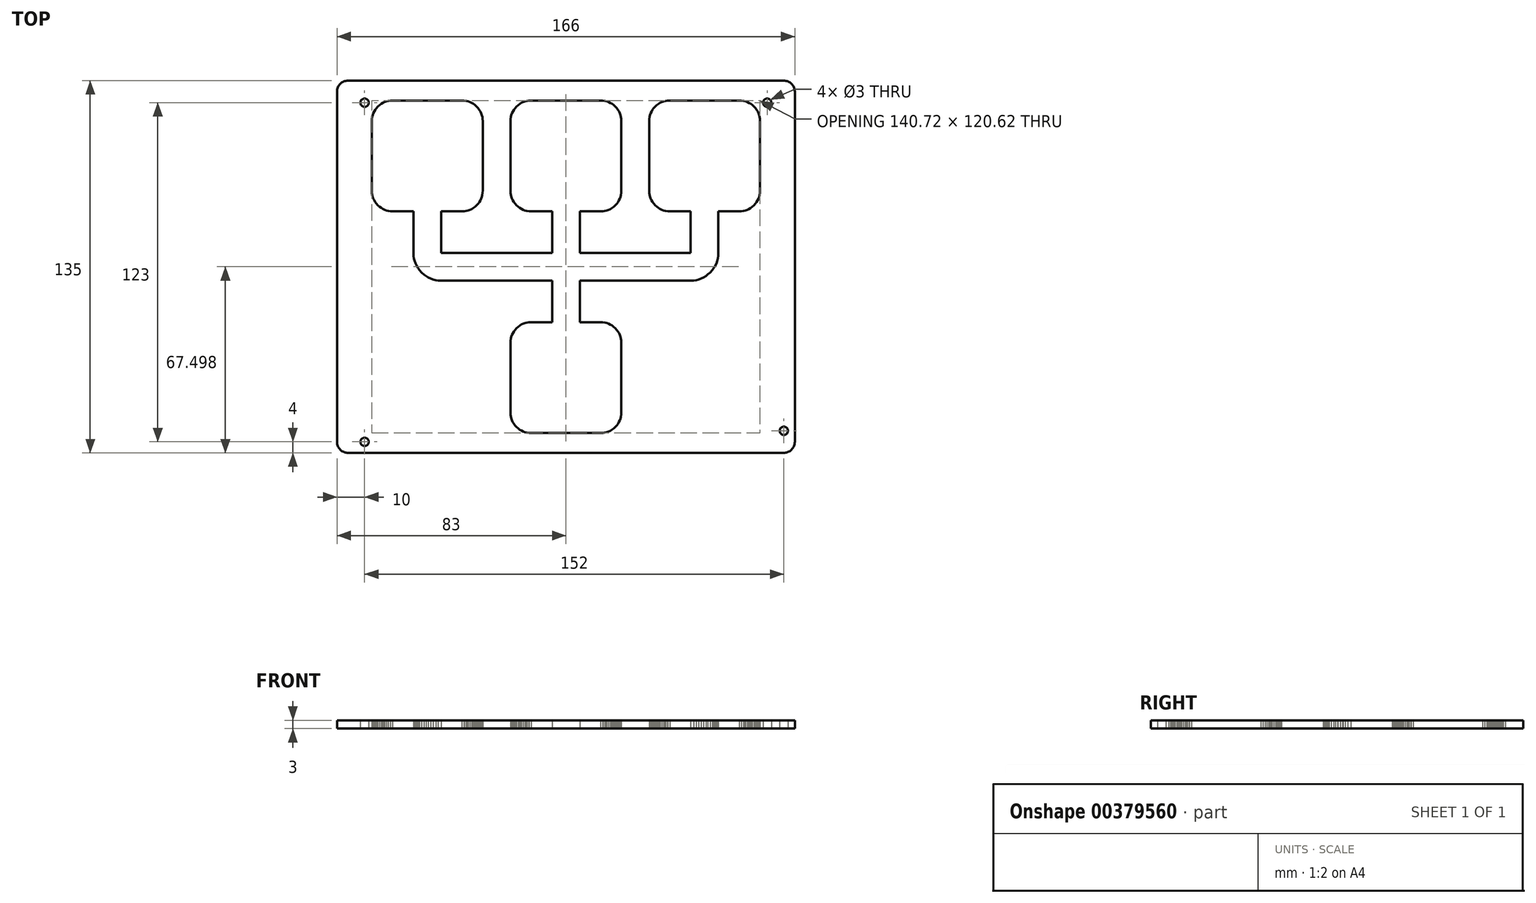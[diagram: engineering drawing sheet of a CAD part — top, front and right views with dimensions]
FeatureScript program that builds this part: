
annotation { "Feature Type Name" : "Feature", "Feature Type Description" : "" }
export const myFeature = defineFeature(function(context is Context, id is Id, definition is map)
    precondition{}
    {
        {
            var Q0;
            Q0=qCreatedBy(makeId("Top.planeOp"),FACE);
            var sketch = newSketch(context, id + "F0", { "sketchPlane" : qUnion([Q0])});
            skLineSegment(sketch, "E0.bottom", {"start": v(79, 67.5) * mm, "end": v(-79, 67.5) * mm});
            skLineSegment(sketch, "E0.top", {"start": v(79, -67.5) * mm, "end": v(-79, -67.5) * mm});
            skLineSegment(sketch, "E0.left", {"start": v(83, 63.5) * mm, "end": v(83, -63.5) * mm});
            skLineSegment(sketch, "E0.right", {"start": v(-83, 63.5) * mm, "end": v(-83, -63.5) * mm});
            skPoint(sketch, "E0.middle", {"position": v(0, 0) * mm});
            skLineSegment(sketch, "E1", {"start": v(0, 86.64) * mm, "end": v(0, -82.26) * mm, "construction": true});
            skLineSegment(sketch, "E2", {"start": v(-88.3, 0) * mm, "end": v(88.19, 0) * mm, "construction": true});
            skPoint(sketch, "E2.endSnap0", {"position": v(-83, 0) * mm});
            skLineSegment(sketch, "E3", {"start": v(-79, 72) * mm, "end": v(-79, -72.22) * mm, "construction": true});
            skLineSegment(sketch, "E4.MirrorCS", {"start": v(79, 72) * mm, "end": v(79, -72.22) * mm, "construction": true});
            skPoint(sketch, "E5.visualSharp", {"position": v(-83, 67.5) * mm});
            skArc(sketch, "E5.filletArc", {"start": v(-79, 67.5) * mm, "mid": v(-81.83, 66.33) * mm, "end": v(-83, 63.5) * mm});
            skPoint(sketch, "E6.visualSharp", {"position": v(83, 67.5) * mm});
            skArc(sketch, "E6.filletArc", {"start": v(83, 63.5) * mm, "mid": v(81.83, 66.33) * mm, "end": v(79, 67.5) * mm});
            skPoint(sketch, "E7.visualSharp", {"position": v(83, -67.5) * mm});
            skArc(sketch, "E7.filletArc", {"start": v(79, -67.5) * mm, "mid": v(81.83, -66.33) * mm, "end": v(83, -63.5) * mm});
            skPoint(sketch, "E8.visualSharp", {"position": v(-83, -67.5) * mm});
            skArc(sketch, "E8.filletArc", {"start": v(-83, -63.5) * mm, "mid": v(-81.83, -66.33) * mm, "end": v(-79, -67.5) * mm});
            skLineSegment(sketch, "E9", {"start": v(-20.1, -52.77) * mm, "end": v(-20.06, -53.63) * mm});
            skLineSegment(sketch, "E10", {"start": v(-20.06, -53.63) * mm, "end": v(-19.96, -54.3) * mm});
            skLineSegment(sketch, "E11", {"start": v(-51.45, -2.81) * mm, "end": v(-50.73, -3.36) * mm});
            skLineSegment(sketch, "E12", {"start": v(-14.73, -20.4) * mm, "end": v(-15.49, -20.66) * mm});
            skLineSegment(sketch, "E13", {"start": v(-19.96, -54.3) * mm, "end": v(-19.8, -54.94) * mm});
            skLineSegment(sketch, "E14", {"start": v(-53.05, -1.2) * mm, "end": v(-52.3, -2.04) * mm});
            skLineSegment(sketch, "E15", {"start": v(-53.6, -0.49) * mm, "end": v(-53.05, -1.2) * mm});
            skLineSegment(sketch, "E16", {"start": v(-54.53, 1.2) * mm, "end": v(-54.15, 0.42) * mm});
            skLineSegment(sketch, "E17", {"start": v(-49.98, -3.82) * mm, "end": v(-49.01, -4.3) * mm});
            skLineSegment(sketch, "E18", {"start": v(-16.08, -20.94) * mm, "end": v(-16.64, -21.28) * mm});
            skLineSegment(sketch, "E19", {"start": v(-18.47, -22.93) * mm, "end": v(-18.87, -23.47) * mm});
            skLineSegment(sketch, "E20", {"start": v(-19.8, -54.94) * mm, "end": v(-19.55, -55.7) * mm});
            skLineSegment(sketch, "E21", {"start": v(-19.27, -56.28) * mm, "end": v(-18.93, -56.85) * mm});
            skLineSegment(sketch, "E22", {"start": v(-15.49, -20.66) * mm, "end": v(-16.08, -20.94) * mm});
            skLineSegment(sketch, "E23", {"start": v(-17.34, -21.79) * mm, "end": v(-17.9, -22.3) * mm});
            skLineSegment(sketch, "E24", {"start": v(-18.93, -56.85) * mm, "end": v(-18.42, -57.55) * mm});
            skLineSegment(sketch, "E25", {"start": v(-55.22, 3.92) * mm, "end": v(-55.1, 3.04) * mm});
            skLineSegment(sketch, "E26", {"start": v(-46.32, -4.97) * mm, "end": v(-45.23, -5.03) * mm});
            skLineSegment(sketch, "E27", {"start": v(-45.23, -5.03) * mm, "end": v(-43.26, -5.03) * mm});
            skLineSegment(sketch, "E28", {"start": v(-43.26, -5.03) * mm, "end": v(-5.03, -5.03) * mm});
            skLineSegment(sketch, "E29", {"start": v(-12.56, -20.1) * mm, "end": v(-13.42, -20.15) * mm});
            skLineSegment(sketch, "E30", {"start": v(-5.03, -5.77) * mm, "end": v(-5.03, -20.1) * mm});
            skLineSegment(sketch, "E31", {"start": v(-19.55, -55.7) * mm, "end": v(-19.27, -56.28) * mm});
            skLineSegment(sketch, "E32", {"start": v(-55.1, 3.04) * mm, "end": v(-54.89, 2.2) * mm});
            skLineSegment(sketch, "E33", {"start": v(-52.3, -2.04) * mm, "end": v(-51.45, -2.81) * mm});
            skLineSegment(sketch, "E34", {"start": v(-5.03, -20.1) * mm, "end": v(-5.4, -20.1) * mm});
            skLineSegment(sketch, "E35", {"start": v(-50.73, -3.36) * mm, "end": v(-49.98, -3.82) * mm});
            skLineSegment(sketch, "E36", {"start": v(-13.42, -20.15) * mm, "end": v(-14.08, -20.24) * mm});
            skLineSegment(sketch, "E37", {"start": v(-17.9, -22.3) * mm, "end": v(-18.47, -22.93) * mm});
            skLineSegment(sketch, "E38", {"start": v(-18.87, -23.47) * mm, "end": v(-19.21, -24.03) * mm});
            skLineSegment(sketch, "E39", {"start": v(-16.64, -21.28) * mm, "end": v(-17.34, -21.79) * mm});
            skLineSegment(sketch, "E40", {"start": v(-54.15, 0.42) * mm, "end": v(-53.6, -0.49) * mm});
            skLineSegment(sketch, "E41", {"start": v(-49.01, -4.3) * mm, "end": v(-48.2, -4.59) * mm});
            skLineSegment(sketch, "E42", {"start": v(-5.03, -5.03) * mm, "end": v(-5.03, -5.77) * mm});
            skLineSegment(sketch, "E43", {"start": v(-54.89, 2.2) * mm, "end": v(-54.53, 1.2) * mm});
            skLineSegment(sketch, "E44", {"start": v(-5.4, -20.1) * mm, "end": v(-12.56, -20.1) * mm});
            skLineSegment(sketch, "E45", {"start": v(-47.2, -4.84) * mm, "end": v(-46.32, -4.97) * mm});
            skLineSegment(sketch, "E46", {"start": v(-14.08, -20.24) * mm, "end": v(-14.73, -20.4) * mm});
            skLineSegment(sketch, "E47", {"start": v(-19.56, -24.75) * mm, "end": v(-19.78, -25.37) * mm});
            skLineSegment(sketch, "E48", {"start": v(-19.78, -25.37) * mm, "end": v(-19.93, -26) * mm});
            skLineSegment(sketch, "E49", {"start": v(-19.93, -26) * mm, "end": v(-20.07, -26.87) * mm});
            skLineSegment(sketch, "E50", {"start": v(-20.07, -26.87) * mm, "end": v(-20.1, -27.64) * mm});
            skLineSegment(sketch, "E51", {"start": v(-20.1, -27.64) * mm, "end": v(-20.1, -28.87) * mm});
            skLineSegment(sketch, "E52", {"start": v(-19.21, -24.03) * mm, "end": v(-19.56, -24.75) * mm});
            skLineSegment(sketch, "E53", {"start": v(-48.2, -4.59) * mm, "end": v(-47.2, -4.84) * mm});
            skLineSegment(sketch, "E54", {"start": v(-20.1, -28.87) * mm, "end": v(-20.1, -52.77) * mm});
            skLineSegment(sketch, "E55", {"start": v(12.56, -60.31) * mm, "end": v(13.42, -60.27) * mm});
            skLineSegment(sketch, "E56", {"start": v(19.93, -54.4) * mm, "end": v(20.07, -53.54) * mm});
            skLineSegment(sketch, "E57", {"start": v(16.74, -21.34) * mm, "end": v(16.18, -21) * mm});
            skLineSegment(sketch, "E58", {"start": v(-13.33, -60.28) * mm, "end": v(-12.56, -60.31) * mm});
            skLineSegment(sketch, "E59", {"start": v(13.42, -60.27) * mm, "end": v(14.09, -60.17) * mm});
            skLineSegment(sketch, "E60", {"start": v(17.34, -58.63) * mm, "end": v(17.9, -58.11) * mm});
            skLineSegment(sketch, "E61", {"start": v(17.9, -22.3) * mm, "end": v(17.28, -21.74) * mm});
            skLineSegment(sketch, "E62", {"start": v(16.64, -59.13) * mm, "end": v(17.34, -58.63) * mm});
            skLineSegment(sketch, "E63", {"start": v(5.03, -5.03) * mm, "end": v(7, -5.03) * mm});
            skLineSegment(sketch, "E64", {"start": v(49.06, -4.27) * mm, "end": v(49.84, -3.9) * mm});
            skLineSegment(sketch, "E65", {"start": v(53.07, -1.2) * mm, "end": v(53.62, -0.47) * mm});
            skLineSegment(sketch, "E66", {"start": v(18.47, -57.48) * mm, "end": v(18.87, -56.95) * mm});
            skLineSegment(sketch, "E67", {"start": v(20.1, -51.54) * mm, "end": v(20.1, -27.64) * mm});
            skLineSegment(sketch, "E68", {"start": v(-17.9, -58.11) * mm, "end": v(-17.27, -58.68) * mm});
            skLineSegment(sketch, "E69", {"start": v(15.46, -20.65) * mm, "end": v(14.84, -20.43) * mm});
            skLineSegment(sketch, "E70", {"start": v(54.08, 0.28) * mm, "end": v(54.55, 1.24) * mm});
            skLineSegment(sketch, "E71", {"start": v(54.55, 1.24) * mm, "end": v(54.84, 2.05) * mm});
            skLineSegment(sketch, "E72", {"start": v(7, -5.03) * mm, "end": v(45.23, -5.03) * mm});
            skLineSegment(sketch, "E73", {"start": v(14.2, -20.28) * mm, "end": v(13.34, -20.14) * mm});
            skLineSegment(sketch, "E74", {"start": v(-16.74, -59.08) * mm, "end": v(-16.18, -59.42) * mm});
            skLineSegment(sketch, "E75", {"start": v(-14.2, -60.14) * mm, "end": v(-13.33, -60.28) * mm});
            skLineSegment(sketch, "E76", {"start": v(-14.84, -59.98) * mm, "end": v(-14.2, -60.14) * mm});
            skLineSegment(sketch, "E77", {"start": v(19.21, -56.38) * mm, "end": v(19.56, -55.66) * mm});
            skLineSegment(sketch, "E78", {"start": v(18.42, -22.87) * mm, "end": v(17.9, -22.3) * mm});
            skLineSegment(sketch, "E79", {"start": v(17.28, -21.74) * mm, "end": v(16.74, -21.34) * mm});
            skLineSegment(sketch, "E80", {"start": v(12.2, -20.1) * mm, "end": v(5.03, -20.1) * mm});
            skLineSegment(sketch, "E81", {"start": v(5.03, -20.1) * mm, "end": v(5.03, -19.37) * mm});
            skLineSegment(sketch, "E82", {"start": v(49.84, -3.9) * mm, "end": v(50.75, -3.34) * mm});
            skLineSegment(sketch, "E83", {"start": v(20.07, -53.54) * mm, "end": v(20.1, -52.77) * mm});
            skLineSegment(sketch, "E84", {"start": v(13.34, -20.14) * mm, "end": v(12.56, -20.1) * mm});
            skLineSegment(sketch, "E85", {"start": v(50.75, -3.34) * mm, "end": v(51.47, -2.8) * mm});
            skLineSegment(sketch, "E86", {"start": v(46.34, -4.97) * mm, "end": v(47.22, -4.84) * mm});
            skLineSegment(sketch, "E87", {"start": v(45.23, -5.03) * mm, "end": v(46.34, -4.97) * mm});
            skLineSegment(sketch, "E88", {"start": v(51.47, -2.8) * mm, "end": v(52.3, -2.04) * mm});
            skLineSegment(sketch, "E89", {"start": v(53.62, -0.47) * mm, "end": v(54.08, 0.28) * mm});
            skLineSegment(sketch, "E90", {"start": v(19.56, -55.66) * mm, "end": v(19.78, -55.05) * mm});
            skLineSegment(sketch, "E91", {"start": v(-15.45, -59.77) * mm, "end": v(-14.84, -59.98) * mm});
            skLineSegment(sketch, "E92", {"start": v(17.9, -58.11) * mm, "end": v(18.47, -57.48) * mm});
            skLineSegment(sketch, "E93", {"start": v(16.08, -59.48) * mm, "end": v(16.64, -59.13) * mm});
            skLineSegment(sketch, "E94", {"start": v(19.78, -55.05) * mm, "end": v(19.93, -54.4) * mm});
            skLineSegment(sketch, "E95", {"start": v(-18.42, -57.55) * mm, "end": v(-17.9, -58.11) * mm});
            skLineSegment(sketch, "E96", {"start": v(-17.27, -58.68) * mm, "end": v(-16.74, -59.08) * mm});
            skLineSegment(sketch, "E97", {"start": v(-16.18, -59.42) * mm, "end": v(-15.45, -59.77) * mm});
            skLineSegment(sketch, "E98", {"start": v(19.81, -25.48) * mm, "end": v(19.55, -24.72) * mm});
            skLineSegment(sketch, "E99", {"start": v(20.1, -27.64) * mm, "end": v(20.06, -26.79) * mm});
            skLineSegment(sketch, "E100", {"start": v(19.55, -24.72) * mm, "end": v(19.27, -24.13) * mm});
            skLineSegment(sketch, "E101", {"start": v(12.56, -20.1) * mm, "end": v(12.2, -20.1) * mm});
            skLineSegment(sketch, "E102", {"start": v(14.09, -60.17) * mm, "end": v(14.73, -60.02) * mm});
            skLineSegment(sketch, "E103", {"start": v(18.87, -56.95) * mm, "end": v(19.21, -56.38) * mm});
            skLineSegment(sketch, "E104", {"start": v(20.06, -26.79) * mm, "end": v(19.97, -26.12) * mm});
            skLineSegment(sketch, "E105", {"start": v(19.97, -26.12) * mm, "end": v(19.81, -25.48) * mm});
            skLineSegment(sketch, "E106", {"start": v(-11.33, -60.31) * mm, "end": v(12.56, -60.31) * mm});
            skLineSegment(sketch, "E107", {"start": v(14.73, -60.02) * mm, "end": v(15.49, -59.75) * mm});
            skLineSegment(sketch, "E108", {"start": v(5.03, -19.37) * mm, "end": v(5.03, -5.03) * mm});
            skLineSegment(sketch, "E109", {"start": v(19.27, -24.13) * mm, "end": v(18.93, -23.57) * mm});
            skLineSegment(sketch, "E110", {"start": v(18.93, -23.57) * mm, "end": v(18.42, -22.87) * mm});
            skLineSegment(sketch, "E111", {"start": v(14.84, -20.43) * mm, "end": v(14.2, -20.28) * mm});
            skLineSegment(sketch, "E112", {"start": v(48.06, -4.63) * mm, "end": v(49.06, -4.27) * mm});
            skLineSegment(sketch, "E113", {"start": v(47.22, -4.84) * mm, "end": v(48.06, -4.63) * mm});
            skLineSegment(sketch, "E114", {"start": v(52.3, -2.04) * mm, "end": v(53.07, -1.2) * mm});
            skLineSegment(sketch, "E115", {"start": v(-12.56, -60.31) * mm, "end": v(-11.33, -60.31) * mm});
            skLineSegment(sketch, "E116", {"start": v(20.1, -52.77) * mm, "end": v(20.1, -51.54) * mm});
            skLineSegment(sketch, "E117", {"start": v(16.18, -21) * mm, "end": v(15.46, -20.65) * mm});
            skLineSegment(sketch, "E118", {"start": v(15.49, -59.75) * mm, "end": v(16.08, -59.48) * mm});
            skLineSegment(sketch, "E119", {"start": v(70.07, 54.93) * mm, "end": v(69.8, 55.7) * mm});
            skLineSegment(sketch, "E120", {"start": v(69.53, 56.28) * mm, "end": v(69.18, 56.84) * mm});
            skLineSegment(sketch, "E121", {"start": v(55.23, 3.94) * mm, "end": v(55.28, 5.02) * mm});
            skLineSegment(sketch, "E122", {"start": v(54.84, 2.05) * mm, "end": v(55.1, 3.07) * mm});
            skLineSegment(sketch, "E123", {"start": v(62.82, 20.1) * mm, "end": v(63.68, 20.15) * mm});
            skLineSegment(sketch, "E124", {"start": v(69.82, 24.75) * mm, "end": v(70.04, 25.37) * mm});
            skLineSegment(sketch, "E125", {"start": v(65.1, 59.98) * mm, "end": v(64.46, 60.14) * mm});
            skLineSegment(sketch, "E126", {"start": v(61.6, 60.3) * mm, "end": v(37.7, 60.3) * mm});
            skLineSegment(sketch, "E127", {"start": v(69.18, 56.84) * mm, "end": v(68.68, 57.55) * mm});
            skLineSegment(sketch, "E128", {"start": v(70.04, 25.37) * mm, "end": v(70.19, 26) * mm});
            skLineSegment(sketch, "E129", {"start": v(66.34, 20.94) * mm, "end": v(66.9, 21.28) * mm});
            skLineSegment(sketch, "E130", {"start": v(55.65, 20.1) * mm, "end": v(62.82, 20.1) * mm});
            skLineSegment(sketch, "E131", {"start": v(35.53, 60.01) * mm, "end": v(34.77, 59.75) * mm});
            skLineSegment(sketch, "E132", {"start": v(34.77, 59.75) * mm, "end": v(34.18, 59.47) * mm});
            skLineSegment(sketch, "E133", {"start": v(64.46, 60.14) * mm, "end": v(63.6, 60.27) * mm});
            skLineSegment(sketch, "E134", {"start": v(32.35, 58.11) * mm, "end": v(31.8, 57.48) * mm});
            skLineSegment(sketch, "E135", {"start": v(30.15, 52.77) * mm, "end": v(30.15, 51.54) * mm});
            skLineSegment(sketch, "E136", {"start": v(30.48, 55.04) * mm, "end": v(30.33, 54.4) * mm});
            skLineSegment(sketch, "E137", {"start": v(64.34, 20.24) * mm, "end": v(64.99, 20.4) * mm});
            skLineSegment(sketch, "E138", {"start": v(70.36, 28.87) * mm, "end": v(70.36, 52.77) * mm});
            skLineSegment(sketch, "E139", {"start": v(64.99, 20.4) * mm, "end": v(65.75, 20.66) * mm});
            skLineSegment(sketch, "E140", {"start": v(65.75, 20.66) * mm, "end": v(66.34, 20.94) * mm});
            skLineSegment(sketch, "E141", {"start": v(70.36, 52.77) * mm, "end": v(70.32, 53.62) * mm});
            skLineSegment(sketch, "E142", {"start": v(67.53, 58.67) * mm, "end": v(67, 59.08) * mm});
            skLineSegment(sketch, "E143", {"start": v(68.16, 58.11) * mm, "end": v(67.53, 58.67) * mm});
            skLineSegment(sketch, "E144", {"start": v(37.7, 60.3) * mm, "end": v(36.84, 60.26) * mm});
            skLineSegment(sketch, "E145", {"start": v(34.18, 59.47) * mm, "end": v(33.62, 59.13) * mm});
            skLineSegment(sketch, "E146", {"start": v(36.17, 60.17) * mm, "end": v(35.53, 60.01) * mm});
            skLineSegment(sketch, "E147", {"start": v(31.05, 56.38) * mm, "end": v(30.7, 55.66) * mm});
            skLineSegment(sketch, "E148", {"start": v(30.7, 55.66) * mm, "end": v(30.48, 55.04) * mm});
            skLineSegment(sketch, "E149", {"start": v(55.28, 5.02) * mm, "end": v(55.28, 5.76) * mm});
            skLineSegment(sketch, "E150", {"start": v(66.9, 21.28) * mm, "end": v(67.6, 21.78) * mm});
            skLineSegment(sketch, "E151", {"start": v(68.16, 22.3) * mm, "end": v(68.73, 22.93) * mm});
            skLineSegment(sketch, "E152", {"start": v(69.8, 55.7) * mm, "end": v(69.53, 56.28) * mm});
            skLineSegment(sketch, "E153", {"start": v(62.82, 60.3) * mm, "end": v(61.6, 60.3) * mm});
            skLineSegment(sketch, "E154", {"start": v(63.6, 60.27) * mm, "end": v(62.82, 60.3) * mm});
            skLineSegment(sketch, "E155", {"start": v(36.84, 60.26) * mm, "end": v(36.17, 60.17) * mm});
            skLineSegment(sketch, "E156", {"start": v(63.68, 20.15) * mm, "end": v(64.34, 20.24) * mm});
            skLineSegment(sketch, "E157", {"start": v(33.62, 59.13) * mm, "end": v(32.92, 58.63) * mm});
            skLineSegment(sketch, "E158", {"start": v(30.15, 51.54) * mm, "end": v(30.15, 27.64) * mm});
            skLineSegment(sketch, "E159", {"start": v(31.8, 57.48) * mm, "end": v(31.39, 56.94) * mm});
            skLineSegment(sketch, "E160", {"start": v(30.15, 27.64) * mm, "end": v(30.2, 26.79) * mm});
            skLineSegment(sketch, "E161", {"start": v(30.3, 26.12) * mm, "end": v(30.45, 25.48) * mm});
            skLineSegment(sketch, "E162", {"start": v(70.36, 27.64) * mm, "end": v(70.36, 28.87) * mm});
            skLineSegment(sketch, "E163", {"start": v(55.28, 20.1) * mm, "end": v(55.65, 20.1) * mm});
            skLineSegment(sketch, "E164", {"start": v(69.13, 23.47) * mm, "end": v(69.47, 24.03) * mm});
            skLineSegment(sketch, "E165", {"start": v(69.47, 24.03) * mm, "end": v(69.82, 24.75) * mm});
            skLineSegment(sketch, "E166", {"start": v(70.22, 54.3) * mm, "end": v(70.07, 54.93) * mm});
            skLineSegment(sketch, "E167", {"start": v(68.68, 57.55) * mm, "end": v(68.16, 58.11) * mm});
            skLineSegment(sketch, "E168", {"start": v(55.28, 5.76) * mm, "end": v(55.28, 20.1) * mm});
            skLineSegment(sketch, "E169", {"start": v(67.6, 21.78) * mm, "end": v(68.16, 22.3) * mm});
            skLineSegment(sketch, "E170", {"start": v(70.33, 26.87) * mm, "end": v(70.36, 27.64) * mm});
            skLineSegment(sketch, "E171", {"start": v(70.32, 53.62) * mm, "end": v(70.22, 54.3) * mm});
            skLineSegment(sketch, "E172", {"start": v(68.73, 22.93) * mm, "end": v(69.13, 23.47) * mm});
            skLineSegment(sketch, "E173", {"start": v(67, 59.08) * mm, "end": v(66.44, 59.42) * mm});
            skLineSegment(sketch, "E174", {"start": v(66.44, 59.42) * mm, "end": v(65.71, 59.76) * mm});
            skLineSegment(sketch, "E175", {"start": v(65.71, 59.76) * mm, "end": v(65.1, 59.98) * mm});
            skLineSegment(sketch, "E176", {"start": v(32.92, 58.63) * mm, "end": v(32.35, 58.11) * mm});
            skLineSegment(sketch, "E177", {"start": v(31.39, 56.94) * mm, "end": v(31.05, 56.38) * mm});
            skLineSegment(sketch, "E178", {"start": v(30.33, 54.4) * mm, "end": v(30.19, 53.54) * mm});
            skLineSegment(sketch, "E179", {"start": v(30.19, 53.54) * mm, "end": v(30.15, 52.77) * mm});
            skLineSegment(sketch, "E180", {"start": v(30.2, 26.79) * mm, "end": v(30.3, 26.12) * mm});
            skLineSegment(sketch, "E181", {"start": v(55.1, 3.07) * mm, "end": v(55.23, 3.94) * mm});
            skLineSegment(sketch, "E182", {"start": v(70.19, 26) * mm, "end": v(70.33, 26.87) * mm});
            skLineSegment(sketch, "E183", {"start": v(15.46, 59.76) * mm, "end": v(14.84, 59.98) * mm});
            skLineSegment(sketch, "E184", {"start": v(14.2, 60.14) * mm, "end": v(13.34, 60.27) * mm});
            skLineSegment(sketch, "E185", {"start": v(31.84, 22.86) * mm, "end": v(32.35, 22.3) * mm});
            skLineSegment(sketch, "E186", {"start": v(17.28, 58.67) * mm, "end": v(16.74, 59.08) * mm});
            skLineSegment(sketch, "E187", {"start": v(5.02, 5.76) * mm, "end": v(5.02, 20.1) * mm});
            skLineSegment(sketch, "E188", {"start": v(14.84, 59.98) * mm, "end": v(14.2, 60.14) * mm});
            skLineSegment(sketch, "E189", {"start": v(13.34, 60.27) * mm, "end": v(12.56, 60.3) * mm});
            skLineSegment(sketch, "E190", {"start": v(32.98, 21.74) * mm, "end": v(33.52, 21.33) * mm});
            skLineSegment(sketch, "E191", {"start": v(19.21, 24.03) * mm, "end": v(19.56, 24.75) * mm});
            skLineSegment(sketch, "E192", {"start": v(31, 24.13) * mm, "end": v(31.33, 23.57) * mm});
            skLineSegment(sketch, "E193", {"start": v(30.71, 24.72) * mm, "end": v(31, 24.13) * mm});
            skLineSegment(sketch, "E194", {"start": v(12.56, 60.3) * mm, "end": v(11.33, 60.3) * mm});
            skLineSegment(sketch, "E195", {"start": v(14.73, 20.4) * mm, "end": v(15.49, 20.66) * mm});
            skLineSegment(sketch, "E196", {"start": v(5.4, 20.1) * mm, "end": v(12.56, 20.1) * mm});
            skLineSegment(sketch, "E197", {"start": v(19.97, 54.3) * mm, "end": v(19.81, 54.93) * mm});
            skLineSegment(sketch, "E198", {"start": v(11.33, 60.3) * mm, "end": v(-12.56, 60.3) * mm});
            skLineSegment(sketch, "E199", {"start": v(-12.56, 60.3) * mm, "end": v(-13.42, 60.26) * mm});
            skLineSegment(sketch, "E200", {"start": v(-13.42, 60.26) * mm, "end": v(-14.08, 60.17) * mm});
            skLineSegment(sketch, "E201", {"start": v(5.02, 20.1) * mm, "end": v(5.4, 20.1) * mm});
            skLineSegment(sketch, "E202", {"start": v(13.42, 20.15) * mm, "end": v(14.09, 20.24) * mm});
            skLineSegment(sketch, "E203", {"start": v(19.55, 55.7) * mm, "end": v(19.27, 56.28) * mm});
            skLineSegment(sketch, "E204", {"start": v(18.42, 57.55) * mm, "end": v(17.9, 58.11) * mm});
            skLineSegment(sketch, "E205", {"start": v(17.9, 58.11) * mm, "end": v(17.28, 58.67) * mm});
            skLineSegment(sketch, "E206", {"start": v(36.06, 20.27) * mm, "end": v(36.92, 20.14) * mm});
            skLineSegment(sketch, "E207", {"start": v(36.92, 20.14) * mm, "end": v(37.7, 20.1) * mm});
            skLineSegment(sketch, "E208", {"start": v(35.42, 20.43) * mm, "end": v(36.06, 20.27) * mm});
            skLineSegment(sketch, "E209", {"start": v(20.1, 27.64) * mm, "end": v(20.1, 28.87) * mm});
            skLineSegment(sketch, "E210", {"start": v(20.1, 52.77) * mm, "end": v(20.06, 53.62) * mm});
            skLineSegment(sketch, "E211", {"start": v(-14.08, 60.17) * mm, "end": v(-14.73, 60.01) * mm});
            skLineSegment(sketch, "E212", {"start": v(45.23, 5.02) * mm, "end": v(43.26, 5.02) * mm});
            skLineSegment(sketch, "E213", {"start": v(-14.73, 60.01) * mm, "end": v(-15.49, 59.75) * mm});
            skLineSegment(sketch, "E214", {"start": v(38.06, 20.1) * mm, "end": v(45.23, 20.1) * mm});
            skLineSegment(sketch, "E215", {"start": v(-15.49, 59.75) * mm, "end": v(-16.07, 59.47) * mm});
            skLineSegment(sketch, "E216", {"start": v(31.33, 23.57) * mm, "end": v(31.84, 22.86) * mm});
            skLineSegment(sketch, "E217", {"start": v(43.26, 5.02) * mm, "end": v(5.02, 5.02) * mm});
            skLineSegment(sketch, "E218", {"start": v(14.09, 20.24) * mm, "end": v(14.73, 20.4) * mm});
            skLineSegment(sketch, "E219", {"start": v(45.23, 20.1) * mm, "end": v(45.23, 19.36) * mm});
            skLineSegment(sketch, "E220", {"start": v(32.35, 22.3) * mm, "end": v(32.98, 21.74) * mm});
            skLineSegment(sketch, "E221", {"start": v(17.34, 21.78) * mm, "end": v(17.9, 22.3) * mm});
            skLineSegment(sketch, "E222", {"start": v(15.49, 20.66) * mm, "end": v(16.08, 20.94) * mm});
            skLineSegment(sketch, "E223", {"start": v(19.93, 26) * mm, "end": v(20.07, 26.87) * mm});
            skLineSegment(sketch, "E224", {"start": v(12.56, 20.1) * mm, "end": v(13.42, 20.15) * mm});
            skLineSegment(sketch, "E225", {"start": v(33.52, 21.33) * mm, "end": v(34.08, 21) * mm});
            skLineSegment(sketch, "E226", {"start": v(45.23, 19.36) * mm, "end": v(45.23, 5.02) * mm});
            skLineSegment(sketch, "E227", {"start": v(30.45, 25.48) * mm, "end": v(30.71, 24.72) * mm});
            skLineSegment(sketch, "E228", {"start": v(17.9, 22.3) * mm, "end": v(18.47, 22.93) * mm});
            skLineSegment(sketch, "E229", {"start": v(37.7, 20.1) * mm, "end": v(38.06, 20.1) * mm});
            skLineSegment(sketch, "E230", {"start": v(5.02, 5.02) * mm, "end": v(5.02, 5.76) * mm});
            skLineSegment(sketch, "E231", {"start": v(18.87, 23.47) * mm, "end": v(19.21, 24.03) * mm});
            skLineSegment(sketch, "E232", {"start": v(20.07, 26.87) * mm, "end": v(20.1, 27.64) * mm});
            skLineSegment(sketch, "E233", {"start": v(20.06, 53.62) * mm, "end": v(19.97, 54.3) * mm});
            skLineSegment(sketch, "E234", {"start": v(16.64, 21.28) * mm, "end": v(17.34, 21.78) * mm});
            skLineSegment(sketch, "E235", {"start": v(18.47, 22.93) * mm, "end": v(18.87, 23.47) * mm});
            skLineSegment(sketch, "E236", {"start": v(19.81, 54.93) * mm, "end": v(19.55, 55.7) * mm});
            skLineSegment(sketch, "E237", {"start": v(34.8, 20.65) * mm, "end": v(35.42, 20.43) * mm});
            skLineSegment(sketch, "E238", {"start": v(19.27, 56.28) * mm, "end": v(18.93, 56.84) * mm});
            skLineSegment(sketch, "E239", {"start": v(18.93, 56.84) * mm, "end": v(18.42, 57.55) * mm});
            skLineSegment(sketch, "E240", {"start": v(16.18, 59.42) * mm, "end": v(15.46, 59.76) * mm});
            skLineSegment(sketch, "E241", {"start": v(19.56, 24.75) * mm, "end": v(19.78, 25.37) * mm});
            skLineSegment(sketch, "E242", {"start": v(19.78, 25.37) * mm, "end": v(19.93, 26) * mm});
            skLineSegment(sketch, "E243", {"start": v(20.1, 28.87) * mm, "end": v(20.1, 52.77) * mm});
            skLineSegment(sketch, "E244", {"start": v(16.08, 20.94) * mm, "end": v(16.64, 21.28) * mm});
            skLineSegment(sketch, "E245", {"start": v(34.08, 21) * mm, "end": v(34.8, 20.65) * mm});
            skLineSegment(sketch, "E246", {"start": v(16.74, 59.08) * mm, "end": v(16.18, 59.42) * mm});
            skLineSegment(sketch, "E247", {"start": v(-19.55, 24.72) * mm, "end": v(-19.27, 24.13) * mm});
            skLineSegment(sketch, "E248", {"start": v(-34.77, 20.66) * mm, "end": v(-34.18, 20.94) * mm});
            skLineSegment(sketch, "E249", {"start": v(-34.18, 20.94) * mm, "end": v(-33.62, 21.28) * mm});
            skLineSegment(sketch, "E250", {"start": v(-35.53, 20.4) * mm, "end": v(-34.77, 20.66) * mm});
            skLineSegment(sketch, "E251", {"start": v(-19.96, 26.12) * mm, "end": v(-19.8, 25.48) * mm});
            skLineSegment(sketch, "E252", {"start": v(-5.03, 5.02) * mm, "end": v(-7, 5.02) * mm});
            skLineSegment(sketch, "E253", {"start": v(-31.39, 23.47) * mm, "end": v(-31.05, 24.03) * mm});
            skLineSegment(sketch, "E254", {"start": v(-30.15, 52.77) * mm, "end": v(-30.2, 53.62) * mm});
            skLineSegment(sketch, "E255", {"start": v(-30.45, 54.93) * mm, "end": v(-30.71, 55.7) * mm});
            skLineSegment(sketch, "E256", {"start": v(-30.71, 55.7) * mm, "end": v(-31, 56.28) * mm});
            skLineSegment(sketch, "E257", {"start": v(-30.19, 26.87) * mm, "end": v(-30.15, 27.64) * mm});
            skLineSegment(sketch, "E258", {"start": v(-31.8, 22.93) * mm, "end": v(-31.39, 23.47) * mm});
            skLineSegment(sketch, "E259", {"start": v(-19.21, 56.38) * mm, "end": v(-19.56, 55.66) * mm});
            skLineSegment(sketch, "E260", {"start": v(-31, 56.28) * mm, "end": v(-31.33, 56.84) * mm});
            skLineSegment(sketch, "E261", {"start": v(-18.93, 23.57) * mm, "end": v(-18.42, 22.86) * mm});
            skLineSegment(sketch, "E262", {"start": v(-30.2, 53.62) * mm, "end": v(-30.3, 54.3) * mm});
            skLineSegment(sketch, "E263", {"start": v(-31.33, 56.84) * mm, "end": v(-31.84, 57.55) * mm});
            skLineSegment(sketch, "E264", {"start": v(-13.33, 20.14) * mm, "end": v(-12.56, 20.1) * mm});
            skLineSegment(sketch, "E265", {"start": v(-17.9, 22.3) * mm, "end": v(-17.27, 21.74) * mm});
            skLineSegment(sketch, "E266", {"start": v(-15.45, 20.65) * mm, "end": v(-14.84, 20.43) * mm});
            skLineSegment(sketch, "E267", {"start": v(-45.23, 5.76) * mm, "end": v(-45.23, 20.1) * mm});
            skLineSegment(sketch, "E268", {"start": v(-7, 5.02) * mm, "end": v(-45.23, 5.02) * mm});
            skLineSegment(sketch, "E269", {"start": v(-16.07, 59.47) * mm, "end": v(-16.64, 59.13) * mm});
            skLineSegment(sketch, "E270", {"start": v(-20.06, 26.79) * mm, "end": v(-19.96, 26.12) * mm});
            skLineSegment(sketch, "E271", {"start": v(-19.8, 25.48) * mm, "end": v(-19.55, 24.72) * mm});
            skLineSegment(sketch, "E272", {"start": v(-16.18, 21) * mm, "end": v(-15.45, 20.65) * mm});
            skLineSegment(sketch, "E273", {"start": v(-45.23, 5.02) * mm, "end": v(-45.23, 5.76) * mm});
            skLineSegment(sketch, "E274", {"start": v(-37.7, 20.1) * mm, "end": v(-36.84, 20.15) * mm});
            skLineSegment(sketch, "E275", {"start": v(-18.47, 57.48) * mm, "end": v(-18.87, 56.94) * mm});
            skLineSegment(sketch, "E276", {"start": v(-17.27, 21.74) * mm, "end": v(-16.74, 21.33) * mm});
            skLineSegment(sketch, "E277", {"start": v(-36.17, 20.24) * mm, "end": v(-35.53, 20.4) * mm});
            skLineSegment(sketch, "E278", {"start": v(-12.2, 20.1) * mm, "end": v(-5.03, 20.1) * mm});
            skLineSegment(sketch, "E279", {"start": v(-12.56, 20.1) * mm, "end": v(-12.2, 20.1) * mm});
            skLineSegment(sketch, "E280", {"start": v(-33.62, 21.28) * mm, "end": v(-32.92, 21.78) * mm});
            skLineSegment(sketch, "E281", {"start": v(-30.7, 24.75) * mm, "end": v(-30.48, 25.37) * mm});
            skLineSegment(sketch, "E282", {"start": v(-16.64, 59.13) * mm, "end": v(-17.34, 58.63) * mm});
            skLineSegment(sketch, "E283", {"start": v(-17.34, 58.63) * mm, "end": v(-17.9, 58.11) * mm});
            skLineSegment(sketch, "E284", {"start": v(-20.1, 52.77) * mm, "end": v(-20.1, 51.54) * mm});
            skLineSegment(sketch, "E285", {"start": v(-16.74, 21.33) * mm, "end": v(-16.18, 21) * mm});
            skLineSegment(sketch, "E286", {"start": v(-31.05, 24.03) * mm, "end": v(-30.7, 24.75) * mm});
            skLineSegment(sketch, "E287", {"start": v(-30.48, 25.37) * mm, "end": v(-30.33, 26) * mm});
            skLineSegment(sketch, "E288", {"start": v(-30.33, 26) * mm, "end": v(-30.19, 26.87) * mm});
            skLineSegment(sketch, "E289", {"start": v(-30.15, 27.64) * mm, "end": v(-30.15, 28.87) * mm});
            skLineSegment(sketch, "E290", {"start": v(-20.07, 53.54) * mm, "end": v(-20.1, 52.77) * mm});
            skLineSegment(sketch, "E291", {"start": v(-19.56, 55.66) * mm, "end": v(-19.78, 55.04) * mm});
            skLineSegment(sketch, "E292", {"start": v(-36.84, 20.15) * mm, "end": v(-36.17, 20.24) * mm});
            skLineSegment(sketch, "E293", {"start": v(-32.35, 22.3) * mm, "end": v(-31.8, 22.93) * mm});
            skLineSegment(sketch, "E294", {"start": v(-30.15, 28.87) * mm, "end": v(-30.15, 52.77) * mm});
            skLineSegment(sketch, "E295", {"start": v(-19.93, 54.4) * mm, "end": v(-20.07, 53.54) * mm});
            skLineSegment(sketch, "E296", {"start": v(-19.78, 55.04) * mm, "end": v(-19.93, 54.4) * mm});
            skLineSegment(sketch, "E297", {"start": v(-14.84, 20.43) * mm, "end": v(-14.2, 20.27) * mm});
            skLineSegment(sketch, "E298", {"start": v(-45.23, 20.1) * mm, "end": v(-44.86, 20.1) * mm});
            skLineSegment(sketch, "E299", {"start": v(-32.92, 21.78) * mm, "end": v(-32.35, 22.3) * mm});
            skLineSegment(sketch, "E300", {"start": v(-30.3, 54.3) * mm, "end": v(-30.45, 54.93) * mm});
            skLineSegment(sketch, "E301", {"start": v(-20.1, 51.54) * mm, "end": v(-20.1, 27.64) * mm});
            skLineSegment(sketch, "E302", {"start": v(-20.1, 27.64) * mm, "end": v(-20.06, 26.79) * mm});
            skLineSegment(sketch, "E303", {"start": v(-18.42, 22.86) * mm, "end": v(-17.9, 22.3) * mm});
            skLineSegment(sketch, "E304", {"start": v(-5.03, 19.36) * mm, "end": v(-5.03, 5.02) * mm});
            skLineSegment(sketch, "E305", {"start": v(-5.03, 20.1) * mm, "end": v(-5.03, 19.36) * mm});
            skLineSegment(sketch, "E306", {"start": v(-44.86, 20.1) * mm, "end": v(-37.7, 20.1) * mm});
            skLineSegment(sketch, "E307", {"start": v(-18.87, 56.94) * mm, "end": v(-19.21, 56.38) * mm});
            skLineSegment(sketch, "E308", {"start": v(-19.27, 24.13) * mm, "end": v(-18.93, 23.57) * mm});
            skLineSegment(sketch, "E309", {"start": v(-14.2, 20.27) * mm, "end": v(-13.33, 20.14) * mm});
            skLineSegment(sketch, "E310", {"start": v(-17.9, 58.11) * mm, "end": v(-18.47, 57.48) * mm});
            skLineSegment(sketch, "E311", {"start": v(-63.6, 20.14) * mm, "end": v(-62.82, 20.1) * mm});
            skLineSegment(sketch, "E312", {"start": v(-70.36, 51.54) * mm, "end": v(-70.36, 27.64) * mm});
            skLineSegment(sketch, "E313", {"start": v(-70.07, 25.48) * mm, "end": v(-69.8, 24.72) * mm});
            skLineSegment(sketch, "E314", {"start": v(-67, 21.33) * mm, "end": v(-66.43, 21) * mm});
            skLineSegment(sketch, "E315", {"start": v(-70.36, 27.64) * mm, "end": v(-70.32, 26.79) * mm});
            skLineSegment(sketch, "E316", {"start": v(-31.84, 57.55) * mm, "end": v(-32.35, 58.11) * mm});
            skLineSegment(sketch, "E317", {"start": v(-68.68, 22.86) * mm, "end": v(-68.16, 22.3) * mm});
            skLineSegment(sketch, "E318", {"start": v(-32.35, 58.11) * mm, "end": v(-32.98, 58.67) * mm});
            skLineSegment(sketch, "E319", {"start": v(-37.7, 60.3) * mm, "end": v(-38.92, 60.3) * mm});
            skLineSegment(sketch, "E320", {"start": v(-55.28, 5.02) * mm, "end": v(-55.22, 3.92) * mm});
            skLineSegment(sketch, "E321", {"start": v(-69.47, 56.38) * mm, "end": v(-69.82, 55.66) * mm});
            skLineSegment(sketch, "E322", {"start": v(-67.6, 58.63) * mm, "end": v(-68.16, 58.11) * mm});
            skLineSegment(sketch, "E323", {"start": v(-66.43, 21) * mm, "end": v(-65.71, 20.65) * mm});
            skLineSegment(sketch, "E324", {"start": v(-70.33, 53.54) * mm, "end": v(-70.36, 52.77) * mm});
            skLineSegment(sketch, "E325", {"start": v(-69.82, 55.66) * mm, "end": v(-70.04, 55.04) * mm});
            skLineSegment(sketch, "E326", {"start": v(-70.04, 55.04) * mm, "end": v(-70.2, 54.4) * mm});
            skLineSegment(sketch, "E327", {"start": v(-55.28, 20.1) * mm, "end": v(-55.28, 19.36) * mm});
            skLineSegment(sketch, "E328", {"start": v(-62.82, 60.3) * mm, "end": v(-63.68, 60.26) * mm});
            skLineSegment(sketch, "E329", {"start": v(-34.8, 59.76) * mm, "end": v(-35.42, 59.98) * mm});
            skLineSegment(sketch, "E330", {"start": v(-70.2, 54.4) * mm, "end": v(-70.33, 53.54) * mm});
            skLineSegment(sketch, "E331", {"start": v(-66.9, 59.13) * mm, "end": v(-67.6, 58.63) * mm});
            skLineSegment(sketch, "E332", {"start": v(-64.34, 60.17) * mm, "end": v(-64.99, 60.01) * mm});
            skLineSegment(sketch, "E333", {"start": v(-38.92, 60.3) * mm, "end": v(-62.82, 60.3) * mm});
            skLineSegment(sketch, "E334", {"start": v(-55.28, 19.36) * mm, "end": v(-55.28, 5.02) * mm});
            skLineSegment(sketch, "E335", {"start": v(-70.32, 26.79) * mm, "end": v(-70.22, 26.12) * mm});
            skLineSegment(sketch, "E336", {"start": v(-36.06, 60.14) * mm, "end": v(-36.92, 60.27) * mm});
            skLineSegment(sketch, "E337", {"start": v(-33.52, 59.08) * mm, "end": v(-34.08, 59.42) * mm});
            skLineSegment(sketch, "E338", {"start": v(-63.68, 60.26) * mm, "end": v(-64.34, 60.17) * mm});
            skLineSegment(sketch, "E339", {"start": v(-69.53, 24.13) * mm, "end": v(-69.18, 23.57) * mm});
            skLineSegment(sketch, "E340", {"start": v(-64.99, 60.01) * mm, "end": v(-65.75, 59.75) * mm});
            skLineSegment(sketch, "E341", {"start": v(-32.98, 58.67) * mm, "end": v(-33.52, 59.08) * mm});
            skLineSegment(sketch, "E342", {"start": v(-35.42, 59.98) * mm, "end": v(-36.06, 60.14) * mm});
            skLineSegment(sketch, "E343", {"start": v(-70.22, 26.12) * mm, "end": v(-70.07, 25.48) * mm});
            skLineSegment(sketch, "E344", {"start": v(-69.13, 56.94) * mm, "end": v(-69.47, 56.38) * mm});
            skLineSegment(sketch, "E345", {"start": v(-65.75, 59.75) * mm, "end": v(-66.34, 59.47) * mm});
            skLineSegment(sketch, "E346", {"start": v(-68.16, 58.11) * mm, "end": v(-68.73, 57.48) * mm});
            skLineSegment(sketch, "E347", {"start": v(-34.08, 59.42) * mm, "end": v(-34.8, 59.76) * mm});
            skLineSegment(sketch, "E348", {"start": v(-69.8, 24.72) * mm, "end": v(-69.53, 24.13) * mm});
            skLineSegment(sketch, "E349", {"start": v(-68.16, 22.3) * mm, "end": v(-67.53, 21.74) * mm});
            skLineSegment(sketch, "E350", {"start": v(-66.34, 59.47) * mm, "end": v(-66.9, 59.13) * mm});
            skLineSegment(sketch, "E351", {"start": v(-69.18, 23.57) * mm, "end": v(-68.68, 22.86) * mm});
            skLineSegment(sketch, "E352", {"start": v(-67.53, 21.74) * mm, "end": v(-67, 21.33) * mm});
            skLineSegment(sketch, "E353", {"start": v(-70.36, 52.77) * mm, "end": v(-70.36, 51.54) * mm});
            skLineSegment(sketch, "E354", {"start": v(-68.73, 57.48) * mm, "end": v(-69.13, 56.94) * mm});
            skLineSegment(sketch, "E355", {"start": v(-65.71, 20.65) * mm, "end": v(-65.1, 20.43) * mm});
            skLineSegment(sketch, "E356", {"start": v(-64.46, 20.27) * mm, "end": v(-63.6, 20.14) * mm});
            skLineSegment(sketch, "E357", {"start": v(-62.82, 20.1) * mm, "end": v(-62.45, 20.1) * mm});
            skLineSegment(sketch, "E358", {"start": v(-65.1, 20.43) * mm, "end": v(-64.46, 20.27) * mm});
            skLineSegment(sketch, "E359", {"start": v(-36.92, 60.27) * mm, "end": v(-37.7, 60.3) * mm});
            skLineSegment(sketch, "E360", {"start": v(-62.45, 20.1) * mm, "end": v(-55.28, 20.1) * mm});
            skLineSegment(sketch, "E361", {"start": v(-73, 77.93) * mm, "end": v(-73, -72.22) * mm, "construction": true});
            skLineSegment(sketch, "E362", {"start": v(-100.38, 59.5) * mm, "end": v(94.03, 59.5) * mm, "construction": true});
            skLineSegment(sketch, "E363.MirrorCS", {"start": v(73, 77.93) * mm, "end": v(73, -72.22) * mm, "construction": true});
            skCircle(sketch, "E364", {"center": v(-73, 59.5) * mm, "radius": 1.5 * mm});
            skCircle(sketch, "E365.MirrorC", {"center": v(73, 59.5) * mm, "radius": 1.5 * mm});
            skCircle(sketch, "E366.MirrorC", {"center": v(-73, -63.5) * mm, "radius": 1.5 * mm});
            skCircle(sketch, "E367.MirrorC", {"center": v(79, -59.5) * mm, "radius": 1.5 * mm});
            skSolve(sketch);
        }
        {
            var Q0;
            Q0=qSketchRegion(id+"F0",true);
            extrude(context, id + "F1", {"entities" : qUnion([Q0]), "depth" : 3 * mm});
        }
    });
